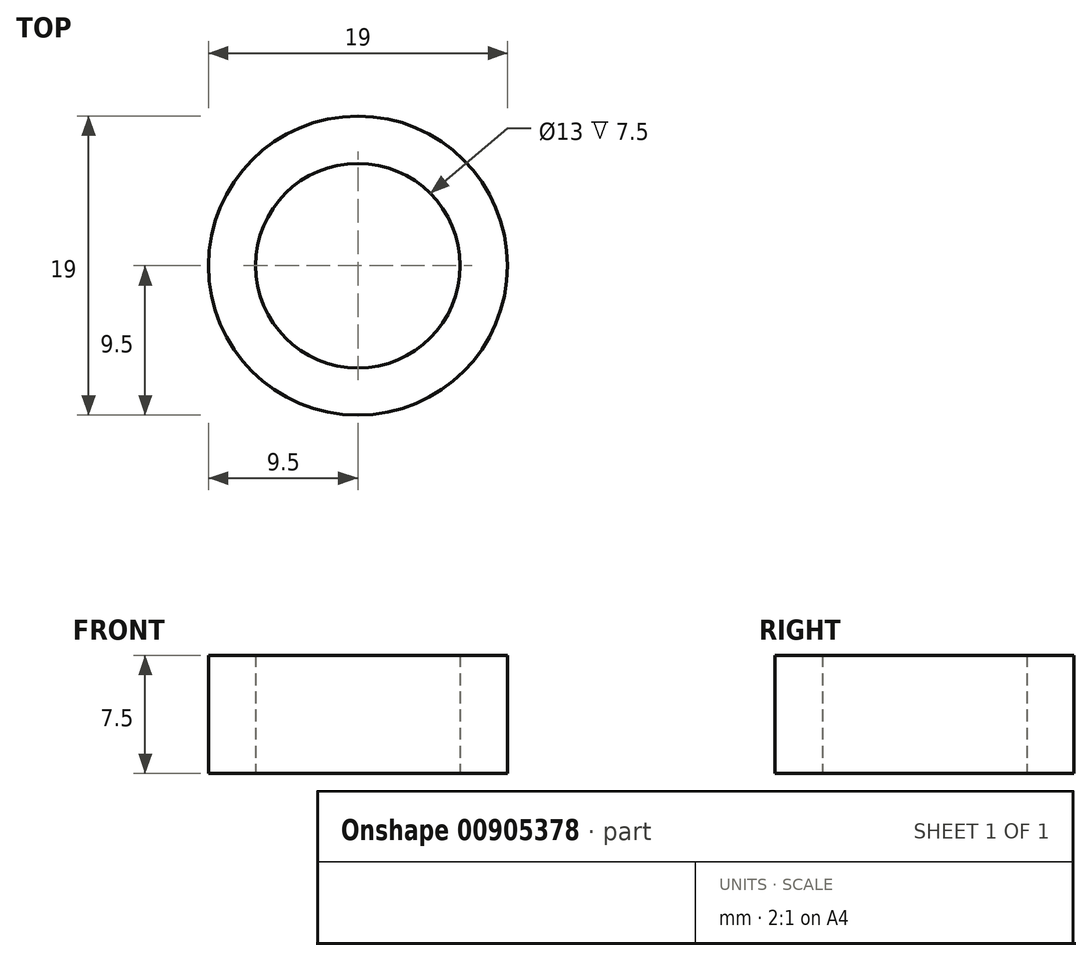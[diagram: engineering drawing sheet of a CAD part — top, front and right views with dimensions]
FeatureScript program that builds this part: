
annotation { "Feature Type Name" : "Feature", "Feature Type Description" : "" }
export const myFeature = defineFeature(function(context is Context, id is Id, definition is map)
    precondition{}
    {
        {
            var Q0;
            Q0=qCreatedBy(makeId("Top.planeOp"),FACE);
            var sketch = newSketch(context, id + "F0", { "sketchPlane" : qUnion([Q0])});
            skCircle(sketch, "E0", {"center": v(0, 0) * mm, "radius": 9.5 * mm});
            skCircle(sketch, "E1", {"center": v(0, 0) * mm, "radius": 6.5 * mm});
            skSolve(sketch);
        }
        {
            var Q0;
            Q0 = qSketchRegion(id + "F0", true);
            extrude(context, id + "F1", {"entities" : qUnion([Q0]), "depth" : 7.5 * mm, "offsetDistance" : 25 * mm});
        }
    });
